# Revit family: P190780JX-162c_JXW8536HS_StainlessSteel_JA_Cooking_Ventilation
name_source: partatom
category: Specialty Equipment
units: mm (PartAtom-declared; Revit-internal decimal feet)

## family parameters
Always vertical = Yes
Cut with Voids When Loaded = No
Enable Cutting in Views = No
Maintain Annotation Orientation = No
Part Type = Normal
Room Calculation Point = No
Round Connector Dimension = Use Diameter
Shared = No
Work Plane-Based = No

## types (1)
- JXW8536HS
    Accent Material = ARCAT - Metal - Steel - Gray
    Amps = 15 A
    Body Material = ARCAT - Metal - Steel - Stainless
    Default Elevation = 0"
    Depth = 19 11/16"
    Description = Lustre Stainless 36" Pyramid Style Canopy Wall Hood
Hotte murale de style pyramidal en acier lustré, 36 po
    Family Name = WALL HOODS - 36"
    Feature 1 = 78,000 BTU Rating
Puissance de 78 000 BTU
    Feature 2 = 600 CFM Blower
Ventilateur de 600 pi³/min
    Feature 3 = Perimetric Extraction
Extraction périmétrique
    Height = 5"
    Installation-Fabrication = http://access.whirlpool.com Instruction&sku=JXW8536HS&language=EN
http://access.whirlpool.com Instruction&sku=JXW8536HS&language=EN
    Manufacturer = Jenn Air
    Model = JXW8536HS
    Voltage = 0 V
    Width = 36"

## geometry (parser evidence)
native form markers: Sweep x3
no freeform markers — native parametric forms only
